# Revit family: Casement_41_D_Side_Hung_SD_Standard
name_source: partatom
category: Windows
revit_build: Autodesk Revit 2014 (Build: 20130308_1515(x64)
units: mm (PartAtom-declared; Revit-internal decimal feet)

## types (6) — shared parameters
Corrected Mullion Configuration = 2 mm  [stored 0.00656168 ft]
Custom Sash Height = 1100 mm  [stored 3.60892 ft]
Custom Window Width = 590 mm  [stored 1.9357 ft]
Description = Window 41mm, Type D, Side hung, Standard sash
Frame Profile Thickness = 41 mm  [stored 0.134514 ft]
Heavy Duty Sash = No
Intruderprufe Insulated U Value = 2.83
Limit Fixed Pane Height Max = 3000 mm  [stored 9.84252 ft]
Limit Fixed Pane Height Min = 200 mm  [stored 0.656168 ft]
Limit Fixed Pane Width Max = 3000 mm  [stored 9.84252 ft]
Limit Fixed Pane Width Min = 200 mm  [stored 0.656168 ft]
Limit Sash Height Max = 1500 mm  [stored 4.92126 ft]
Limit Sash Height Min = 300 mm  [stored 0.984252 ft]
Limit Sash Width Max = 700 mm  [stored 2.29659 ft]
Limit Sash Width Min = 300 mm  [stored 0.984252 ft]
Limit Window Width Min = 388 mm
Manufacturer = Crealco
Max System DG Unit Thickness = 25 mm  [stored 0.082021 ft]
Model = Casement 41
Rough Width = 3 mm  [stored 0.00984252 ft]
Sash Side Gap = 44 mm
Standard Mullion Different = No
Standard Sash = Yes
URL = http://www.crealco.co.za
Wall Closure = By host
zero-valued in all types: Custom Frame Offset From Exterior

## per-type parameters (varying)
| type | Clearvue Insulated LowE SHGC Value | Clearvue Insulated LowE U Value | Clearvue Insulated SHGC Value | Clearvue Insulated U Value | Clearvue SHGC Value | Clearvue U Value | Custom Windload | Custom Window Height | Energy Advantage SHGC Value | Energy Advantage U Value | Intruderprufe Insulated LowE SHGC Value | Intruderprufe Insulated LowE U Value | Intruderprufe Insulated SHGC Value | Intruderprufe LowE SHGC Value | Intruderprufe LowE U Value | Intruderprufe SHGC Value | Intruderprufe U Value | Toughened Safety SHGC Value | Toughened Safety U Value |
| 41-0615S-SD-1000Pa | 0.787 | 4.13 | 0.787 | 4.17 | 0.498 | 6.14 | 1000 mm  [stored 3.28084 ft] | 1490 mm  [stored 4.88845 ft] | 0.449 | 5.14 | 0.653 | 2.79 | 0.653 | 0.418 | 5 | 0.47 | 6.01 | 0.498 | 6.14 |
| 41-0615S-SD-1500Pa | 0.787 | 4.13 | 0.787 | 4.17 | 0.498 | 6.14 | 1500 mm  [stored 4.92126 ft] | 1490 mm  [stored 4.88845 ft] | 0.449 | 5.14 | 0.653 | 2.79 | 0.653 | 0.418 | 5 | 0.47 | 6.01 | 0.498 | 6.14 |
| 41-0615S-SD-2000Pa | 0.787 | 4.13 | 0.787 | 4.17 | 0.498 | 6.14 | 2000 mm  [stored 6.56168 ft] | 1490 mm  [stored 4.88845 ft] | 0.449 | 5.14 | 0.653 | 2.79 | 0.653 | 0.418 | 5 | 0.47 | 6.01 | 0.498 | 6.14 |
| 41-0618S-SD-1000Pa | 0.797 | 4.21 | 0.797 | 4.25 | 0.531 | 6.12 | 1000 mm  [stored 3.28084 ft] | 1790 mm  [stored 5.8727 ft] | 0.478 | 5.01 | 0.662 | 2.8 | 0.662 | 0.444 | 4.86 | 0.5 | 5.97 | 0.531 | 6.12 |
| 41-0618S-SD-1500Pa | 0.797 | 4.21 | 0.797 | 4.25 | 0.531 | 6.12 | 1500 mm  [stored 4.92126 ft] | 1790 mm  [stored 5.8727 ft] | 0.478 | 5.01 | 0.662 | 2.8 | 0.662 | 0.444 | 4.86 | 0.5 | 5.97 | 0.531 | 6.12 |
| 41-0618S-SD-2000Pa | 0.797 | 4.21 | 0.797 | 4.25 | 0.531 | 6.12 | 2000 mm  [stored 6.56168 ft] | 1790 mm  [stored 5.8727 ft] | 0.478 | 5.01 | 0.662 | 2.8 | 0.662 | 0.444 | 4.86 | 0.5 | 5.97 | 0.531 | 6.12 |

note: [stored X ft] marks values corroborated as IEEE doubles in the binary element streams (Revit-internal decimal feet)

## geometry (parser evidence)
native form markers: Sweep x15
no freeform markers — native parametric forms only
